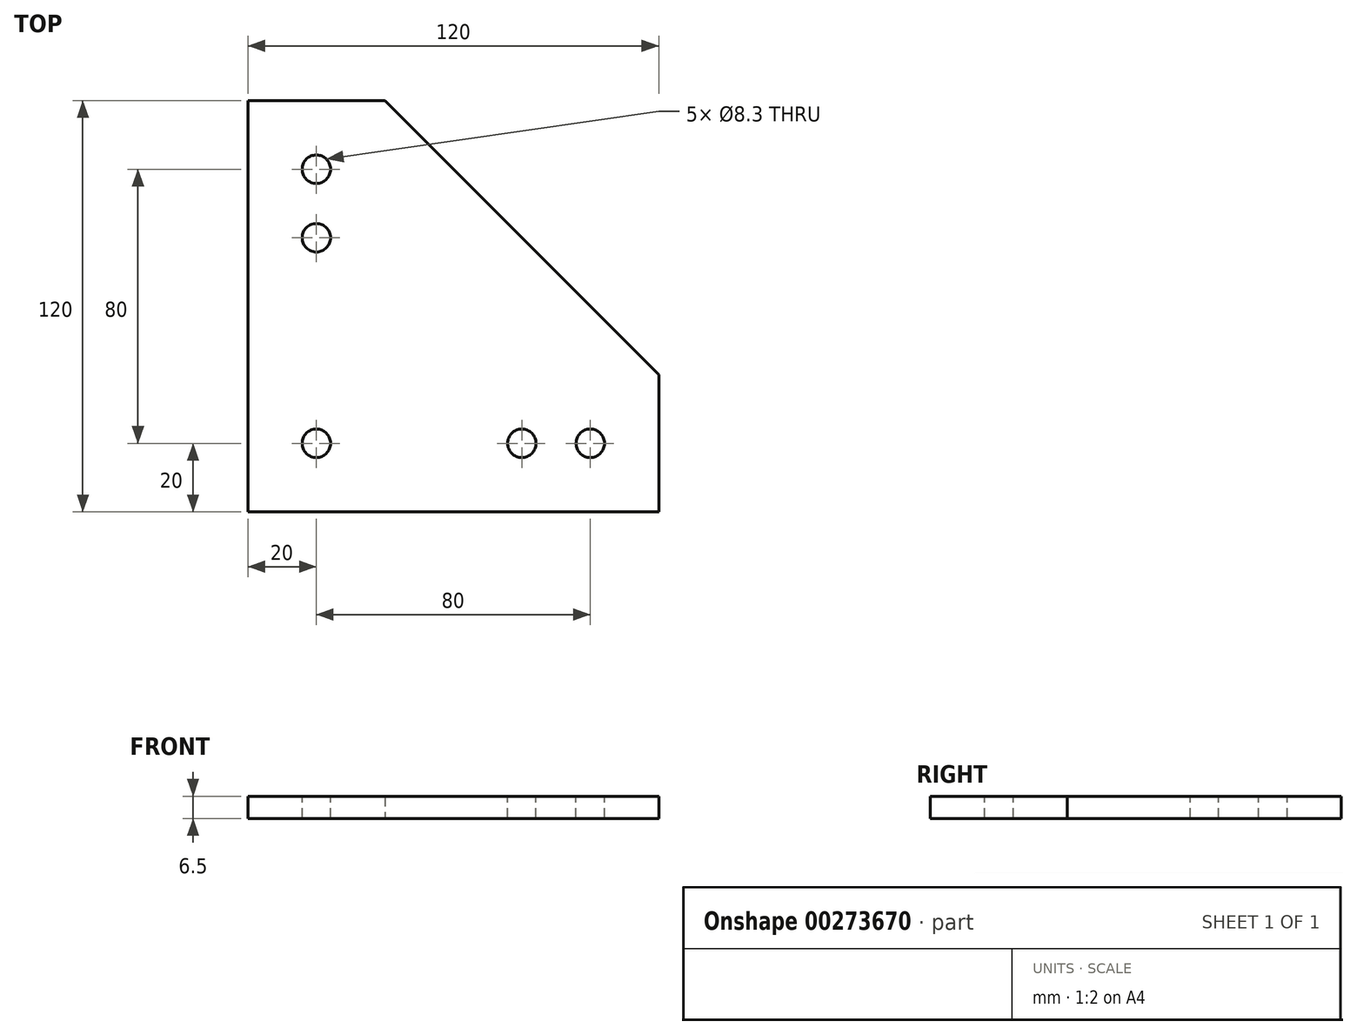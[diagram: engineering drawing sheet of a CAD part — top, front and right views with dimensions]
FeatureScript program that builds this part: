
annotation { "Feature Type Name" : "Feature", "Feature Type Description" : "" }
export const myFeature = defineFeature(function(context is Context, id is Id, definition is map)
    precondition{}
    {
        {
            var Q0;
            Q0=qCreatedBy(makeId("Top.planeOp"),FACE);
            var sketch = newSketch(context, id + "F0", { "sketchPlane" : qUnion([Q0])});
            skLineSegment(sketch, "E0", {"start": v(-100, 20) * mm, "end": v(-20, 100) * mm, "construction": true});
            skLineSegment(sketch, "E1", {"start": v(20, 100) * mm, "end": v(100, 20) * mm});
            skLineSegment(sketch, "E2", {"start": v(100, -20) * mm, "end": v(20, -100) * mm, "construction": true});
            skLineSegment(sketch, "E3", {"start": v(-20, -100) * mm, "end": v(-100, -20) * mm, "construction": true});
            skLineSegment(sketch, "E4", {"start": v(-20, 100) * mm, "end": v(20, 100) * mm});
            skLineSegment(sketch, "E5", {"start": v(-100, -20) * mm, "end": v(-100, 20) * mm, "construction": true});
            skLineSegment(sketch, "E6", {"start": v(100, 20) * mm, "end": v(100, -20) * mm});
            skLineSegment(sketch, "E7", {"start": v(-20, -100) * mm, "end": v(20, -100) * mm, "construction": true});
            skPoint(sketch, "E8.orphan", {"position": v(0, 120) * mm});
            skPoint(sketch, "E9.orphan", {"position": v(120, 0) * mm});
            skPoint(sketch, "E10.orphan", {"position": v(0, -120) * mm});
            skPoint(sketch, "E11.orphan", {"position": v(-120, 0) * mm});
            skLineSegment(sketch, "E12", {"start": v(-20, 100) * mm, "end": v(-20, -20) * mm});
            skLineSegment(sketch, "E13", {"start": v(100, -20) * mm, "end": v(-20, -20) * mm});
            skSolve(sketch);
        }
        {
            var Q0;
            Q0=qSketchRegion(id+"F0",true);
            extrude(context, id + "F1", {"entities" : qUnion([Q0]), "depth" : 6.5 * mm});
        }
        {
            var Q0;
            Q0=makeQuery(id+"F1.opExtrude","CAP_FACE",FACE,{"disambiguationData":[OSD([sQuery(id+"F0.wireOp",EDGE,"E0"),sQuery(id+"F0.wireOp",EDGE,"E1"),sQuery(id+"F0.wireOp",EDGE,"E2"),sQuery(id+"F0.wireOp",EDGE,"E3"),sQuery(id+"F0.wireOp",EDGE,"E4"),sQuery(id+"F0.wireOp",EDGE,"E5"),sQuery(id+"F0.wireOp",EDGE,"E6"),sQuery(id+"F0.wireOp",EDGE,"E7")])],"isStart":false});
            var sketch = newSketch(context, id + "F2", { "sketchPlane" : qUnion([Q0])});
            skPoint(sketch, "E14", {"position": v(0, 80) * mm});
            skPoint(sketch, "E15", {"position": v(80, 0) * mm});
            skLineSegment(sketch, "E16.bottom", {"start": v(-20, -20) * mm, "end": v(20, -20) * mm, "construction": true});
            skLineSegment(sketch, "E16.top", {"start": v(-20, 20) * mm, "end": v(20, 20) * mm, "construction": true});
            skLineSegment(sketch, "E16.left", {"start": v(-20, -20) * mm, "end": v(-20, 20) * mm, "construction": true});
            skLineSegment(sketch, "E16.right", {"start": v(20, -20) * mm, "end": v(20, 20) * mm, "construction": true});
            skCircle(sketch, "E17", {"center": v(0, 42.5) * mm, "radius": 8.5 * mm, "construction": true});
            skCircle(sketch, "E18", {"center": v(42.5, 0) * mm, "radius": 8.5 * mm, "construction": true});
            skLineSegment(sketch, "E19", {"start": v(0, 80) * mm, "end": v(0, 0) * mm, "construction": true});
            skLineSegment(sketch, "E20", {"start": v(0, 0) * mm, "end": v(80, 0) * mm, "construction": true});
            skPoint(sketch, "E21", {"position": v(0, 60) * mm});
            skPoint(sketch, "E22", {"position": v(60, 0) * mm});
            skPoint(sketch, "E23", {"position": v(0, 0) * mm});
            skSolve(sketch);
        }
        {
            var Q0;
            Q0=sQuery(id+"F2.wireOp",VERTEX,"E14");
            var Q1;
            Q1=sQuery(id+"F2.wireOp",VERTEX,"E21");
            var Q2;
            Q2=sQuery(id+"F2.wireOp",VERTEX,"E23");
            var Q3;
            Q3=sQuery(id+"F2.wireOp",VERTEX,"E22");
            var Q4;
            Q4=sQuery(id+"F2.wireOp",VERTEX,"E20.end");
            var Q5;
            Q5=makeQuery(id+"F1.opExtrude","SWEPT_BODY",BODY,{"disambiguationData":[OSD([sQuery(id+"F0.wireOp",EDGE,"E0"),sQuery(id+"F0.wireOp",EDGE,"E1"),sQuery(id+"F0.wireOp",EDGE,"E2"),sQuery(id+"F0.wireOp",EDGE,"E3"),sQuery(id+"F0.wireOp",EDGE,"E4"),sQuery(id+"F0.wireOp",EDGE,"E5"),sQuery(id+"F0.wireOp",EDGE,"E6"),sQuery(id+"F0.wireOp",EDGE,"E7")])]});
            hole(context, id + "F3", {"style" : HoleStyle.SIMPLE, "endStyle" : HoleEndStyle.THROUGH, "standardTappedOrClearance" : lookupTablePath({ "standard" : "ISO", "size" : "8.3", "type" : "Drilled" }), "standardBlindInLast" : lookupTablePath({ "standard" : "ISO", "size" : "8.3", "type" : "Drilled" }), "holeDiameter" : 8.3 * mm, "tappedDepth" : 12 * mm, "tapClearance" : 3, "locations" : qUnion([Q0, Q1, Q2, Q3, Q4]), "scope" : qUnion([Q5])});
        }
    });
